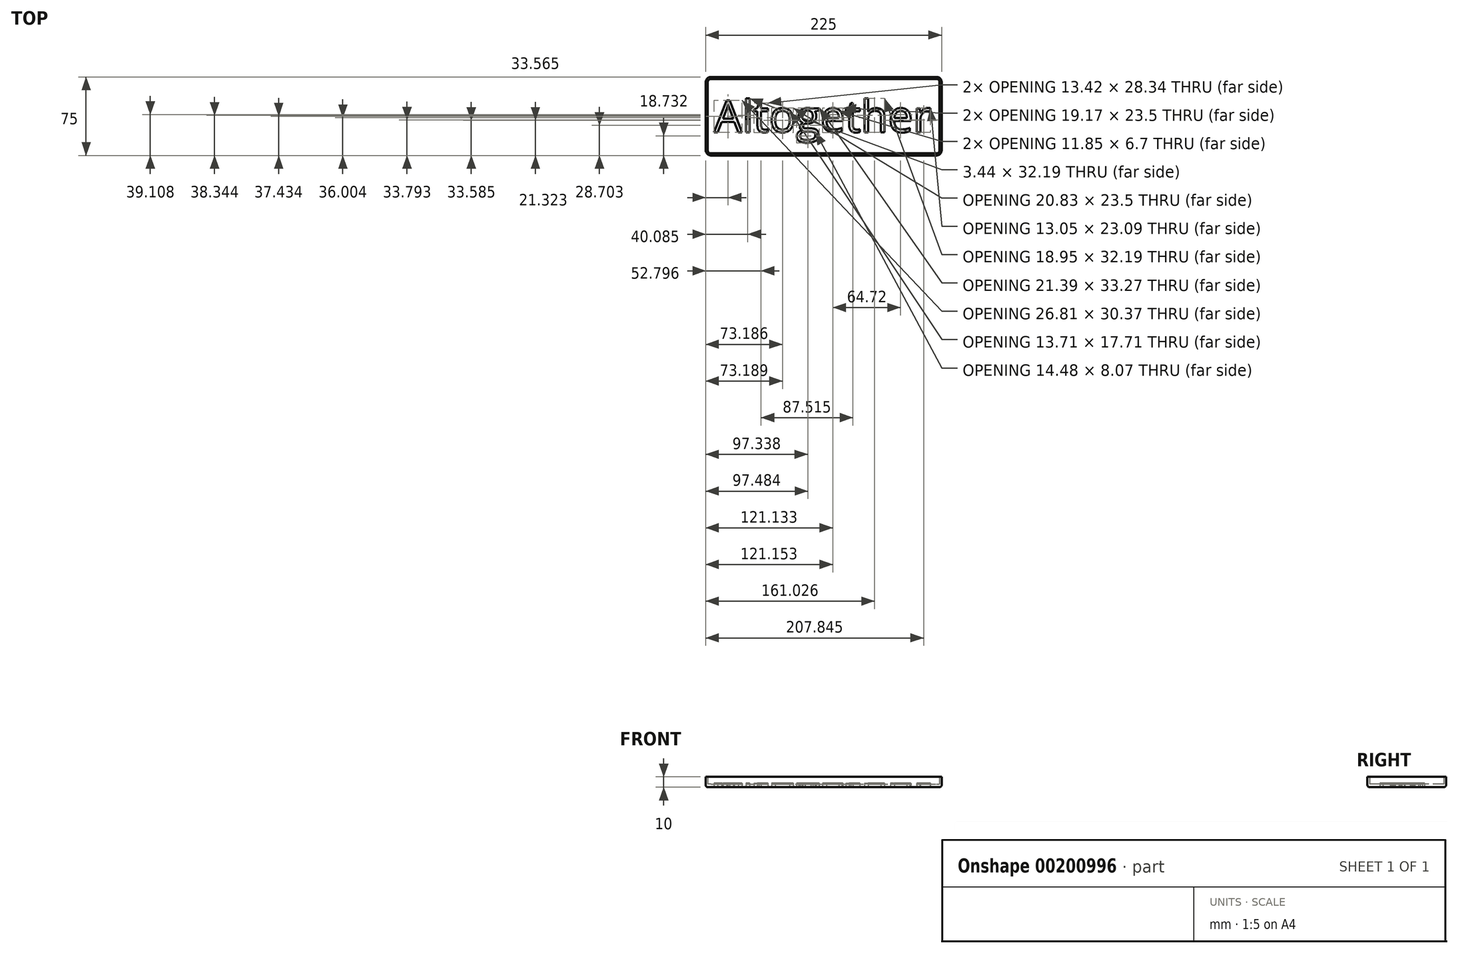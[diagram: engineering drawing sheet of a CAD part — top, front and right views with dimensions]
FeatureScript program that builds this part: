
annotation { "Feature Type Name" : "Feature", "Feature Type Description" : "" }
export const myFeature = defineFeature(function(context is Context, id is Id, definition is map)
    precondition{}
    {
        {
            var Q0;
            Q0=qCreatedBy(makeId("Top.planeOp"),FACE);
            var sketch = newSketch(context, id + "F0", { "sketchPlane" : qUnion([Q0])});
            skLineSegment(sketch, "E0.bottom", {"start": v(-37.46, 75) * mm, "end": v(177.54, 75) * mm});
            skLineSegment(sketch, "E0.top", {"start": v(-37.46, 0) * mm, "end": v(177.54, 0) * mm});
            skLineSegment(sketch, "E0.left", {"start": v(-42.46, 70) * mm, "end": v(-42.46, 5) * mm});
            skLineSegment(sketch, "E0.right", {"start": v(182.54, 70) * mm, "end": v(182.54, 5) * mm});
            skLineSegment(sketch, "E1.0", {"start": v(-37.46, 2) * mm, "end": v(177.54, 2) * mm});
            skLineSegment(sketch, "E1.1", {"start": v(-40.46, 70) * mm, "end": v(-40.46, 5) * mm});
            skLineSegment(sketch, "E1.2", {"start": v(-37.46, 73) * mm, "end": v(177.54, 73) * mm});
            skLineSegment(sketch, "E1.3", {"start": v(180.54, 70) * mm, "end": v(180.54, 5) * mm});
            skLineSegment(sketch, "E2", {"start": v(70.04, 73) * mm, "end": v(70.04, 2) * mm, "construction": true});
            skText(sketch, "E3", { "text": "Altogether", "fontName": "OpenSans-Regular.ttf"});
            skLineSegment(sketch, "E4", {"start": v(174.62, 37.5) * mm, "end": v(-34.54, 37.5) * mm, "construction": true});
            skLineSegment(sketch, "E5", {"start": v(70.04, 37.5) * mm, "end": v(180.54, 37.5) * mm, "construction": true});
            skPoint(sketch, "E6.visualSharp", {"position": v(180.54, 73) * mm});
            skArc(sketch, "E6.filletArc", {"start": v(180.54, 70) * mm, "mid": v(179.66, 72.12) * mm, "end": v(177.54, 73) * mm});
            skPoint(sketch, "E7.visualSharp", {"position": v(-40.46, 73) * mm});
            skArc(sketch, "E7.filletArc", {"start": v(-37.46, 73) * mm, "mid": v(-39.58, 72.12) * mm, "end": v(-40.46, 70) * mm});
            skPoint(sketch, "E8.visualSharp", {"position": v(-40.46, 2) * mm});
            skArc(sketch, "E8.filletArc", {"start": v(-40.46, 5) * mm, "mid": v(-39.58, 2.88) * mm, "end": v(-37.46, 2) * mm});
            skPoint(sketch, "E9.visualSharp", {"position": v(180.54, 2) * mm});
            skArc(sketch, "E9.filletArc", {"start": v(177.54, 2) * mm, "mid": v(179.66, 2.88) * mm, "end": v(180.54, 5) * mm});
            skPoint(sketch, "E10.visualSharp", {"position": v(182.54, 0) * mm});
            skArc(sketch, "E10.filletArc", {"start": v(177.54, 0) * mm, "mid": v(181.08, 1.46) * mm, "end": v(182.54, 5) * mm});
            skPoint(sketch, "E11.visualSharp", {"position": v(182.54, 75) * mm});
            skArc(sketch, "E11.filletArc", {"start": v(182.54, 70) * mm, "mid": v(181.08, 73.54) * mm, "end": v(177.54, 75) * mm});
            skPoint(sketch, "E12.visualSharp", {"position": v(-42.46, 75) * mm});
            skArc(sketch, "E12.filletArc", {"start": v(-37.46, 75) * mm, "mid": v(-41, 73.54) * mm, "end": v(-42.46, 70) * mm});
            skPoint(sketch, "E13.visualSharp", {"position": v(-42.46, 0) * mm});
            skArc(sketch, "E13.filletArc", {"start": v(-42.46, 5) * mm, "mid": v(-41, 1.46) * mm, "end": v(-37.46, 0) * mm});
            const initialGuessF0  = {"E3": [-0.03454, 0.02225, 1, 0, 0.0305]};
            skSetInitialGuess(sketch, initialGuessF0);
            skSolve(sketch);
        }
        {
            var Q0;
            Q0=makeQuery(id+"F0.imprint","IMPRINT",FACE,{"disambiguationData":[TD([[makeQuery(id+"F0.imprint","IMPRINT",EDGE,{"derivedFrom":sQuery(id+"F0.wireOp",EDGE,"E1.0")}),1.0]])]});
            var Q1;
            Q1=makeQuery(id+"F0.imprint","IMPRINT",FACE,{"disambiguationData":[TD([[makeQuery(id+"F0.imprint","IMPRINT",EDGE,{"derivedFrom":sQuery(id+"F0.wireOp",EDGE,"E3.sketch_text.stroke-63")}),1.0]])]});
            var Q2;
            Q2=makeQuery(id+"F0.imprint","IMPRINT",FACE,{"disambiguationData":[TD([[makeQuery(id+"F0.imprint","IMPRINT",EDGE,{"derivedFrom":sQuery(id+"F0.wireOp",EDGE,"E3.sketch_text.stroke-17")}),1.0]])]});
            var Q3;
            Q3=makeQuery(id+"F0.imprint","IMPRINT",FACE,{"disambiguationData":[TD([[makeQuery(id+"F0.imprint","IMPRINT",EDGE,{"derivedFrom":sQuery(id+"F0.wireOp",EDGE,"E3.sketch_text.stroke-8")}),1.0]])]});
            var Q4;
            Q4=makeQuery(id+"F0.imprint","IMPRINT",FACE,{"disambiguationData":[TD([[makeQuery(id+"F0.imprint","IMPRINT",EDGE,{"derivedFrom":sQuery(id+"F0.wireOp",EDGE,"E3.sketch_text.stroke-45")}),1.0]])]});
            var Q5;
            Q5=makeQuery(id+"F0.imprint","IMPRINT",FACE,{"disambiguationData":[TD([[makeQuery(id+"F0.imprint","IMPRINT",EDGE,{"derivedFrom":sQuery(id+"F0.wireOp",EDGE,"E3.sketch_text.stroke-82")}),1.0]])]});
            var Q6;
            Q6=makeQuery(id+"F0.imprint","IMPRINT",FACE,{"disambiguationData":[TD([[makeQuery(id+"F0.imprint","IMPRINT",EDGE,{"derivedFrom":sQuery(id+"F0.wireOp",EDGE,"E3.sketch_text.stroke-91")}),1.0]])]});
            var Q7;
            Q7=makeQuery(id+"F0.imprint","IMPRINT",FACE,{"disambiguationData":[TD([[makeQuery(id+"F0.imprint","IMPRINT",EDGE,{"derivedFrom":sQuery(id+"F0.wireOp",EDGE,"E3.sketch_text.stroke-111")}),1.0]])]});
            var Q8;
            Q8=makeQuery(id+"F0.imprint","IMPRINT",FACE,{"disambiguationData":[TD([[makeQuery(id+"F0.imprint","IMPRINT",EDGE,{"derivedFrom":sQuery(id+"F0.wireOp",EDGE,"E3.sketch_text.stroke-167")}),1.0]])]});
            extrude(context, id + "F1", {"entities" : qUnion([Q0, Q1, Q2, Q3, Q4, Q5, Q6, Q7, Q8]), "depth" : 3 * mm});
        }
        {
            var Q0;
            Q0=makeQuery(id+"F0.imprint","IMPRINT",FACE,{"disambiguationData":[TD([[makeQuery(id+"F0.imprint","IMPRINT",EDGE,{"derivedFrom":sQuery(id+"F0.wireOp",EDGE,"E0.bottom")}),-1.0]])]});
            extrude(context, id + "F2", {"entities" : qUnion([Q0]), "operationType" : NewBodyOperationType.ADD, "depth" : 10 * mm});
        }
        {
            var Q0;
            Q0=makeQuery(id+"F0.imprint","IMPRINT",FACE,{"disambiguationData":[TD([[makeQuery(id+"F0.imprint","IMPRINT",EDGE,{"derivedFrom":sQuery(id+"F0.wireOp",EDGE,"E3.sketch_text.stroke-0")}),-1.0]])]});
            var Q1;
            Q1=makeQuery(id+"F0.imprint","IMPRINT",FACE,{"disambiguationData":[TD([[makeQuery(id+"F0.imprint","IMPRINT",EDGE,{"derivedFrom":sQuery(id+"F0.wireOp",EDGE,"E3.sketch_text.stroke-8")}),-1.0]])]});
            var Q2;
            Q2=makeQuery(id+"F0.imprint","IMPRINT",FACE,{"disambiguationData":[TD([[makeQuery(id+"F0.imprint","IMPRINT",EDGE,{"derivedFrom":sQuery(id+"F0.wireOp",EDGE,"E3.sketch_text.stroke-25")}),-1.0]])]});
            var Q3;
            Q3=makeQuery(id+"F0.imprint","IMPRINT",FACE,{"disambiguationData":[TD([[makeQuery(id+"F0.imprint","IMPRINT",EDGE,{"derivedFrom":sQuery(id+"F0.wireOp",EDGE,"E3.sketch_text.stroke-44")}),-1.0]])]});
            var Q4;
            Q4=makeQuery(id+"F0.imprint","IMPRINT",FACE,{"disambiguationData":[TD([[makeQuery(id+"F0.imprint","IMPRINT",EDGE,{"derivedFrom":sQuery(id+"F0.wireOp",EDGE,"E3.sketch_text.stroke-71")}),-1.0]])]});
            var Q5;
            Q5=makeQuery(id+"F0.imprint","IMPRINT",FACE,{"disambiguationData":[TD([[makeQuery(id+"F0.imprint","IMPRINT",EDGE,{"derivedFrom":sQuery(id+"F0.wireOp",EDGE,"E3.sketch_text.stroke-13")}),-1.0]])]});
            var Q6;
            Q6=makeQuery(id+"F0.imprint","IMPRINT",FACE,{"disambiguationData":[TD([[makeQuery(id+"F0.imprint","IMPRINT",EDGE,{"derivedFrom":sQuery(id+"F0.wireOp",EDGE,"E3.sketch_text.stroke-97")}),-1.0]])]});
            var Q7;
            Q7=makeQuery(id+"F0.imprint","IMPRINT",FACE,{"disambiguationData":[TD([[makeQuery(id+"F0.imprint","IMPRINT",EDGE,{"derivedFrom":sQuery(id+"F0.wireOp",EDGE,"E3.sketch_text.stroke-116")}),-1.0]])]});
            var Q8;
            Q8=makeQuery(id+"F0.imprint","IMPRINT",FACE,{"disambiguationData":[TD([[makeQuery(id+"F0.imprint","IMPRINT",EDGE,{"derivedFrom":sQuery(id+"F0.wireOp",EDGE,"E3.sketch_text.stroke-135")}),-1.0]])]});
            var Q9;
            Q9=makeQuery(id+"F0.imprint","IMPRINT",FACE,{"disambiguationData":[TD([[makeQuery(id+"F0.imprint","IMPRINT",EDGE,{"derivedFrom":sQuery(id+"F0.wireOp",EDGE,"E3.sketch_text.stroke-153")}),-1.0]])]});
            var Q10;
            Q10=makeQuery(id+"F0.imprint","IMPRINT",FACE,{"disambiguationData":[TD([[makeQuery(id+"F0.imprint","IMPRINT",EDGE,{"derivedFrom":sQuery(id+"F0.wireOp",EDGE,"E3.sketch_text.stroke-172")}),-1.0]])]});
            extrude(context, id + "F3", {"entities" : qUnion([Q0, Q1, Q2, Q3, Q4, Q5, Q6, Q7, Q8, Q9, Q10]), "depth" : 4 * mm});
        }
        {
            var Q0;
            Q0=makeQuery(id+"F2.opExtrude","CAP_EDGE",EDGE,{"disambiguationData":[OSD([sQuery(id+"F0.wireOp",EDGE,"E0.bottom")])],"isStart":true});
            fillet(context, id + "F4", {"entities" : qUnion([Q0]), "radius" : 2 * mm, "tangentPropagation" : true, "allowEdgeOverflow" : false});
        }
    });
